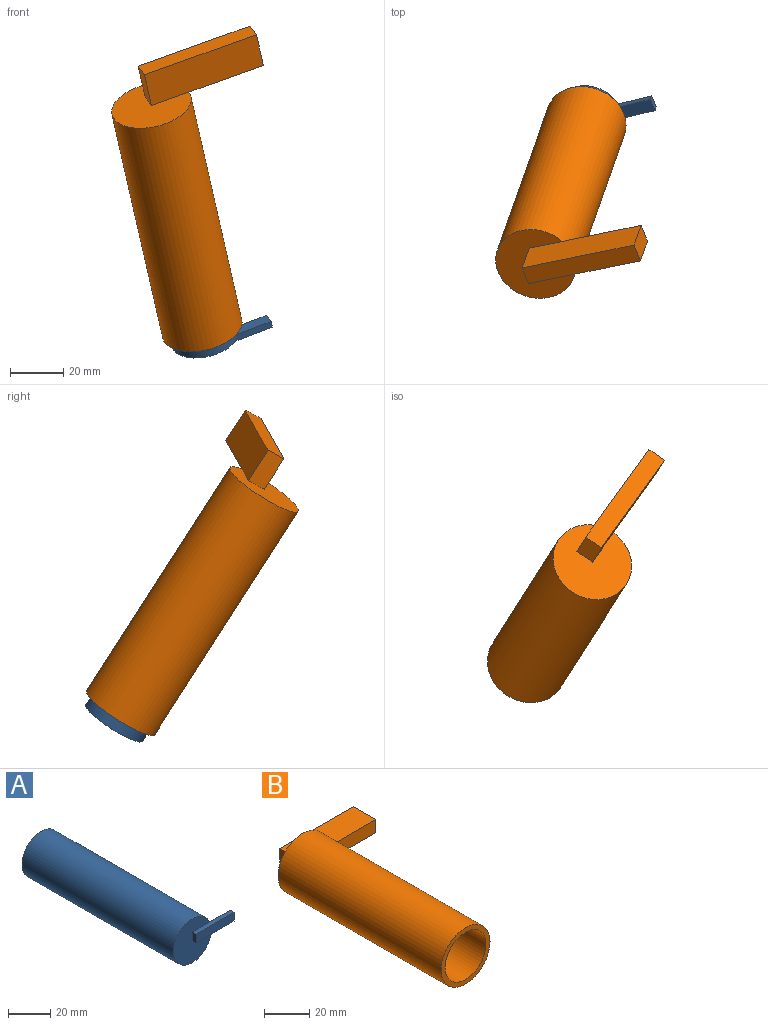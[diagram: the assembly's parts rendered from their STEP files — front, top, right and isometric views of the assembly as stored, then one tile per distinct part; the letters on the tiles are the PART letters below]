
ASSEMBLY  parts=2 mates=1
PART A: 9 faces, bbox 38.1x104.1x25.4 mm
  f0: plane 25.4x25.4mm, normal (0,-1,0), area 444mm2, adj f1,f4,f5,f6
  f1: cylinder r=12.7mm len=101.6mm, axis (0,1,0), area 8107.3mm2, adj f0,f2,f3
  f2: plane 25.4x25.4mm, normal (0,1,0), area 506.7mm2, adj f1
  f3: plane 13.76x5.08mm, normal (0,1,0), area 66.3mm2, adj f1,f4,f6,f7
  f4: plane 25.4x2.54mm, normal (0,0,1), area 64.5mm2, adj f0,f3,f5,f7,f8
  f5: plane 5.08x2.54mm, normal (-1,0,0), area 12.9mm2, adj f0,f4,f6,f8
  f6: plane 25.4x2.54mm, normal (0,0,-1), area 64.5mm2, adj f0,f3,f5,f7,f8
  f7: plane 5.08x2.54mm, normal (1,0,0), area 12.9mm2, adj f3,f4,f6,f8
  f8: plane 25.4x5.08mm, normal (0,-1,0), area 129mm2, adj f4,f5,f6,f7
PART B: 11 faces, bbox 60.8x115.6x30.5 mm
  f0: cylinder r=15.24mm len=101.6mm, axis (0,1,0), area 9728.8mm2, adj f1,f2,f9
  f1: plane 30.48x30.48mm, normal (0,-1,0), area 223mm2, adj f0,f3
  f2: plane 30.48x30.48mm, normal (0,1,0), area 624.7mm2, adj f0,f5,f6,f7
  f3: cylinder r=12.7mm len=99.06mm, axis (0,1,0), area 7904.6mm2, adj f1,f4
  f4: plane 25.4x25.4mm, normal (0,-1,0), area 506.7mm2, adj f3
  f5: plane 45.53x14mm, normal (0,0,-1), area 637.3mm2, adj f2,f6,f8,f9,f10
  f6: plane 14x7.16mm, normal (-1,0,0), area 100.2mm2, adj f2,f5,f7,f10
  f7: plane 45.53x14mm, normal (0,0,1), area 637.3mm2, adj f2,f6,f8,f9,f10
  f8: plane 14x7.16mm, normal (1,0,0), area 100.2mm2, adj f5,f7,f9,f10
  f9: plane 32.08x7.16mm, normal (0,-1,0), area 221.1mm2, adj f0,f5,f7,f8
  f10: plane 45.53x7.16mm, normal (0,1,0), area 326.1mm2, adj f5,f6,f7,f8
PLACE A rot(axis=(0.97,0.01,0.24),122.1deg) t=(75.01,-413.09,-55.45)mm
PLACE B rot(axis=(0.98,0,0.22),122.1deg) t=(74.14,-415.56,-51.61)mm
MATE cylindrical B.f0 <-> A.f1  axis (-0.19,-0.53,0.83) through (93.23,-361.62,-135.57)mm
